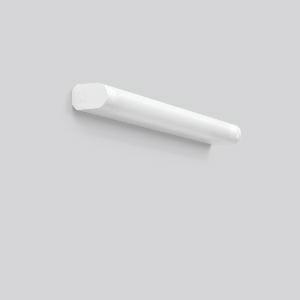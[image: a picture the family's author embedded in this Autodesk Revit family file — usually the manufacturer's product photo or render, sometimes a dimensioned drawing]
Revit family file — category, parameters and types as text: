
# Revit family: rt_44_451174_002_d4f0
name_source: partatom
category: Lighting Fixtures
units: mm (PartAtom-declared; Revit-internal decimal feet)

## family parameters
Cut with Voids When Loaded = No
Host = Face
Light Source = No
Part Type = Normal
Room Calculation Point = No
Round Connector Dimension = Use Diameter
Shared = No

## types (1)
- RT 44 (1 x LED Modul 830, 920 lm, 3000)
    Apparent Load = 10 VA
    CIE Flux Codes = 36 64 85 81 100
    Color Rendering = 80
    Color Temperature = 3000
    Default Elevation = 1800 mm
    Description = Series: RT 44
Linear luminaire, can be used as wall and mirror luminaire. Base: aluminium, powder-coated. End caps: plastic (polycarbonate), shock-resistant. Diffuser: plastic (polycarbonate), opal. Suitable for Ceiling mounting, Wall (surface). Can be installed horizontally and vertically. Very easy installation thanks to Plug+Play connection. With push button switch and Schukoplug socket. Driver integrated. High type of protection: IP44 for use in wet areas. 
Colour: pure white (RAL 9010)
Length: 721 mm
Width: 55 mm
Height: 87 mm
Lamp: LED
Socket: without socket
Colour temperature: 3000K
Colour rendering index (CRI): 80
System power: 10 W
Rated luminous flux: 920 lm
Luminous efficiency: 92 lm/W
Control gear: Regulated power supply
Protection class: I
Type of protection: IP 44
    Height = 87 mm
    Lamp = 1 x LED Modul 830
    Lamp Light Flux = 920 lm
    Lamp count = 1
    Length = 721 mm
    Lifetime = 50000 h
    Luminous efficacy = 92 lm/W
    Manufacturer = RZB
    ModVariant = No
    Model = 451174.002
    Mounting Place = Ceiling, Wall
    Mounting Type = Surface mounted
    Number of Poles = 1
    OnlyDefault = Yes
    Power Factor = 1
    Product Name = RT 44
    Product group = Surface mounted ceiling and wall luminaires
    ProductGroupID = 305
    Protection Class = Protection class I
    Protection Degree = IP 44
    RLX_Detail_Level = 1
    RLX_Emergency_Light_Flux = 0 lm
    RLX_Emergency_Type = 0
    RLX_Emergency_Type_DB = No
    RlxData = <blob elided: 25973 chars, md5=33167172>
    Socket = socket
    Standby Power = 0 W
    System Light Flux = 920 lm
    System Power = 10 W
    Type Comments = Product without accessories
    Type Image = 451060.752.jpg
    URL = http://relux.com
    VarID = ---
    Voltage = 230 V
    Voltage Range = 220-240 V
    Weight = 0.00 kg
    Width = 55 mm

## geometry (parser evidence)
native form markers: Blend x4, Sweep x13
no freeform markers — native parametric forms only
